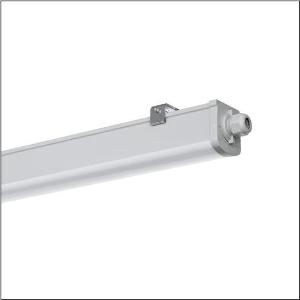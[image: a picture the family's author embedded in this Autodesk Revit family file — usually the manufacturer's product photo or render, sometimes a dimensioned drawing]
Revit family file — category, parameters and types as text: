
# Revit family: monsun_r__31_51fa207p460b_ddf4
name_source: partatom
category: Lighting Fixtures
units: mm (PartAtom-declared; Revit-internal decimal feet)

## family parameters
Cut with Voids When Loaded = No
Host = Face
Light Source = No
Part Type = Normal
Room Calculation Point = No
Round Connector Dimension = Use Diameter
Shared = No

## types (1)
- Monsun® 31 (1 x LED, 6700 lm, 50 W, 4000K)
    Apparent Load = 50 VA
    CIE Flux Codes = 42 72 91 92 100
    Color Rendering = 80
    Color Temperature = 4000K
    Default Elevation = 1800 mm
    Description = Monsun® 31, damp-proof luminaire, primary optical cover: diffuser, of PC, frosted, light emission: direct distribution, primary light characteristic: symmetric, installation type: surface-mounted, LED, rated luminous flux: 6.700lm, luminous efficacy: 134lm/W, light colour: 840, colour temperature: 4000K, control gear: ECG, with terminal, 3+1-pole, max. 2.5mm², through-wiring: 3x 2.5mm² + 1x 1.5mm², mains connection: 220..240V, AC, 50/60Hz, rated input power: 50W, housing, luminaire housing, of PC, light grey (RAL 7035), length: 1.458mm, width: 68mm, height: 76mm, protection rating (complete): IP66, insulation class (complete): insulation class II (safety insulation), certification: CE, ENEC, UKCA, protection symbol: D, impact resistance: IK08, permissible operating ambient temperature: -20..+40°C, corresponds to IFS (International Featured Standards) requirements for safety and quality in the food industry, contact your sales advisor before using the luminaires in applications with unclear chemical exposure, large temperature fluctuations or condensation-forming humidity, packaging unit: 1 piece
    Height = 77 mm
    Lamp = 1 x LED
    Lamp Light Flux = 6700 lm
    Lamp Power = 50 W
    Lamp count = 1
    Length = 1518 mm
    Luminous efficacy = 134 lm/W
    Manufacturer = Siteco
    ModVariant = No
    Model = 51FA207P460B
    Mounting Place = Ceiling
    Mounting Type = Surface mounted
    Number of Poles = 1
    OnlyDefault = Yes
    Power Factor = 1
    Product Name = Monsun® 31
    Product group = damp-proof luminaire
    ProductGroupID = 301
    Protection Class = Protection class II
    Protection Degree = IP 66
    RLX_Detail_Level = 1
    RLX_Emergency_Light_Flux = 0 lm
    RLX_Emergency_Type = 0
    RLX_Emergency_Type_DB = No
    RlxData = <blob elided: 33101 chars, md5=29844ace>
    Socket = socket
    Standby Power = 0 W
    System Light Flux = 6700 lm
    System Power = 50 W
    Type Comments = Product without accessories
    Type Image = l_1006174.jpg
    URL = http://relux.com
    VarID = ---
    Voltage = 0 V
    Weight = 0.00 kg
    Width = 69 mm

## geometry (parser evidence)
native form markers: Blend x4, Sweep x11
no freeform markers — native parametric forms only
